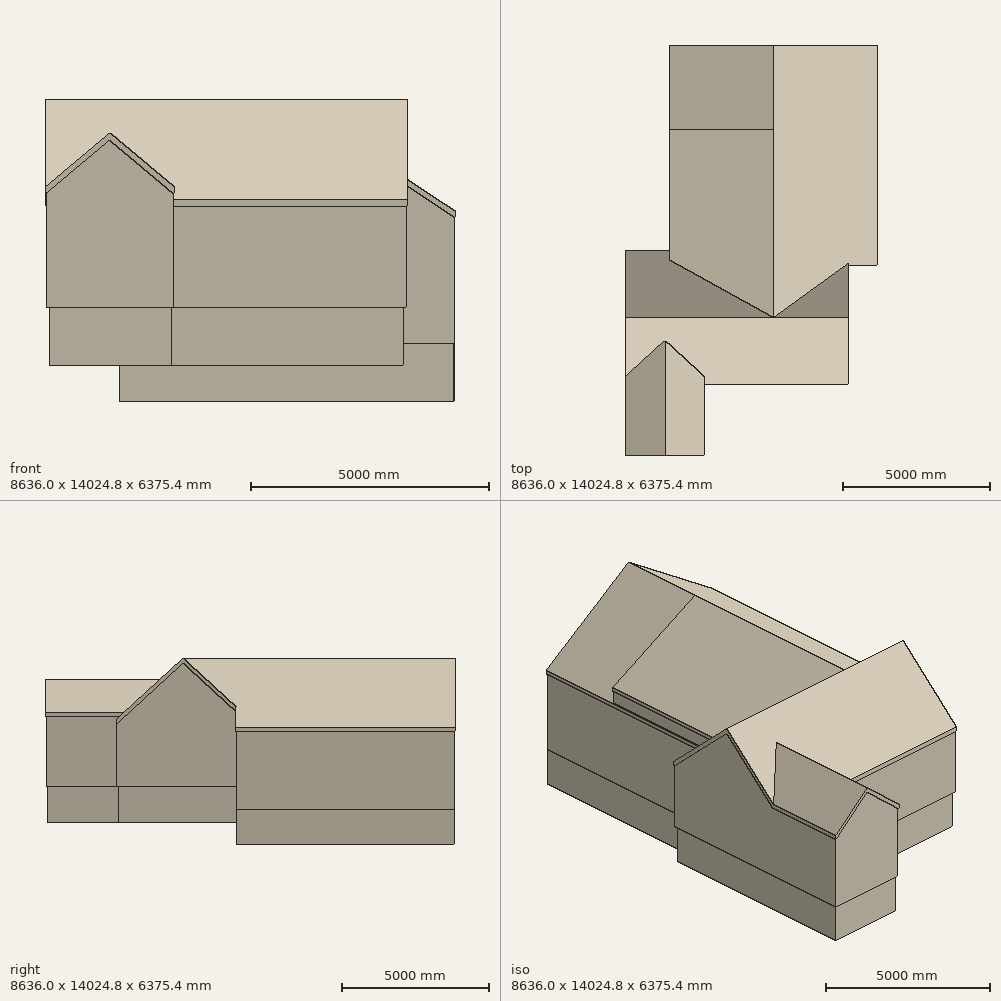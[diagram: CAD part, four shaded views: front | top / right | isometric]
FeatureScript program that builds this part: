
annotation { "Feature Type Name" : "Feature", "Feature Type Description" : "" }
export const myFeature = defineFeature(function(context is Context, id is Id, definition is map)
    precondition{}
    {
        {
            var Q0;
            Q0=qCreatedBy(makeId("Front.planeOp"),FACE);
            var sketch = newSketch(context, id + "F0", { "sketchPlane" : qUnion([Q0])});
            skLineSegment(sketch, "E0", {"start": v(0, 0) * mm, "end": v(0, 2540) * mm});
            skLineSegment(sketch, "E1", {"start": v(0, 2540) * mm, "end": v(1362.17, 3683) * mm});
            skLineSegment(sketch, "E2", {"start": v(1362.17, 3683) * mm, "end": v(2724.35, 2540) * mm});
            skLineSegment(sketch, "E3", {"start": v(2724.35, 2540) * mm, "end": v(2724.35, 0) * mm});
            skLineSegment(sketch, "E4", {"start": v(2724.35, 0) * mm, "end": v(0, 0) * mm});
            skSolve(sketch);
        }
        {
            var Q0;
            Q0 = qSketchRegion(id + "F0", true);
            extrude(context, id + "F1", {"entities" : qUnion([Q0]), "oppositeDirection" : true, "depth" : 3911.6 * mm});
        }
        {
            var Q0;
            Q0=makeQuery(id+"F1.opExtrude","SWEPT_FACE",FACE,{"disambiguationData":[OSD([sQuery(id+"F0.wireOp",EDGE,"E0")])]});
            var sketch = newSketch(context, id + "F2", { "sketchPlane" : qUnion([Q0])});
            skLineSegment(sketch, "E5", {"start": v(-7014.4, 2286) * mm, "end": v(-7014.4, 0) * mm});
            skLineSegment(sketch, "E6", {"start": v(-7014.4, 0) * mm, "end": v(-2413, 0) * mm});
            skLineSegment(sketch, "E7", {"start": v(-2413, 0) * mm, "end": v(-2413, 2286) * mm});
            skLineSegment(sketch, "E8", {"start": v(-2413, 2286) * mm, "end": v(-4713.7, 4394.2) * mm});
            skLineSegment(sketch, "E9", {"start": v(-4713.7, 4394.2) * mm, "end": v(-7014.4, 2286) * mm});
            skSolve(sketch);
        }
        {
            var Q0;
            Q0 = qSketchRegion(id + "F2", true);
            extrude(context, id + "F3", {"entities" : qUnion([Q0]), "operationType" : NewBodyOperationType.ADD, "oppositeDirection" : true, "depth" : 7620 * mm});
        }
        {
            var Q0;
            Q0=makeQuery(id+"F3.opExtrude","SWEPT_FACE",FACE,{"disambiguationData":[OSD([sQuery(id+"F2.wireOp",EDGE,"E5")])]});
            var sketch = newSketch(context, id + "F4", { "sketchPlane" : qUnion([Q0])});
            skLineSegment(sketch, "E10", {"start": v(-1524, -762) * mm, "end": v(-1524, 2032) * mm});
            skLineSegment(sketch, "E11", {"start": v(-1524, 2032) * mm, "end": v(-5080, 4394.2) * mm});
            skLineSegment(sketch, "E12", {"start": v(-5080, 4394.2) * mm, "end": v(-8636, 2032) * mm});
            skLineSegment(sketch, "E13", {"start": v(-8636, 2032) * mm, "end": v(-8636, -762) * mm});
            skLineSegment(sketch, "E14", {"start": v(-8636, -762) * mm, "end": v(-1524, -762) * mm});
            skSolve(sketch);
        }
        {
            var Q0;
            Q0 = qSketchRegion(id + "F4", true);
            var Q1;
            Q1=makeQuery(id+"F3.opExtrude","CAP_VERTEX",VERTEX,{"disambiguationData":[OSD([sQuery(id+"F2.wireOp",EDGE,"zL3uoyGX-favN-0fO6-DJR6-y5zJvDEcZm2G"),sQuery(id+"F2.wireOp",EDGE,"UiKADa09-KCoQ-Akzb-1IEs-Xu5JY1OC5VxY")])],"isStart":false});
            extrude(context, id + "F5", {"entities" : qUnion([Q0]), "operationType" : NewBodyOperationType.ADD, "depth" : 7010.4 * mm});
        }
        {
            var Q0;
            Q0=makeQuery(id+"F5.opExtrude","CAP_FACE",FACE,{"disambiguationData":[OSD([sQuery(id+"F4.wireOp",EDGE,"E10"),sQuery(id+"F4.wireOp",EDGE,"E11"),sQuery(id+"F4.wireOp",EDGE,"E12"),sQuery(id+"F4.wireOp",EDGE,"E13"),sQuery(id+"F4.wireOp",EDGE,"E14")])],"isStart":true});
            extrude(context, id + "F6", {"entities" : qUnion([Q0]), "operationType" : NewBodyOperationType.ADD, "depth" : 508 * mm});
        }
        {
            var Q0;
            {var subQ0=sQuery(id+"F4.wireOp",EDGE,"E12");var subQ1=sQuery(id+"F4.wireOp",EDGE,"E11");Q0=makeQuery(id+"F6.boolean.opBoolean","SPLIT",FACE,{"disambiguationData":[TD([makeQuery(id+"F3.opExtrude","SWEPT_FACE",FACE,{"disambiguationData":[OSD([sQuery(id+"F2.wireOp",EDGE,"E9")])]})])],"derivedFrom":makeQuery(id+"F6.opExtrude","CAP_FACE",FACE,{"disambiguationData":[OSD([sQuery(id+"F4.wireOp",EDGE,"E10"),subQ1,subQ0,sQuery(id+"F4.wireOp",EDGE,"E13"),sQuery(id+"F4.wireOp",EDGE,"E14")])],"isStart":false})});}
            var Q1;
            Q1=makeQuery(id+"F3.opExtrude","CAP_VERTEX",VERTEX,{"disambiguationData":[OSD([sQuery(id+"F2.wireOp",EDGE,"E8"),sQuery(id+"F2.wireOp",EDGE,"E9")])],"isStart":false});
            extrude(context, id + "F7", {"entities" : qUnion([Q0]), "operationType" : NewBodyOperationType.ADD, "endBound" : BoundingType.UP_TO_VERTEX, "endBoundEntityVertex" : qUnion([Q1]), "depth" : 25.4 * mm});
        }
        {
            var Q0;
            Q0=makeQuery(id+"F3.boolean.opBoolean","MERGE",FACE,{"derivedFrom":[makeQuery(id+"F1.opExtrude","SWEPT_FACE",FACE,{"disambiguationData":[OSD([sQuery(id+"F0.wireOp",EDGE,"E0")])]}),makeQuery(id+"F3.opExtrude","CAP_FACE",FACE,{"disambiguationData":[OSD([sQuery(id+"F2.wireOp",EDGE,"E5"),sQuery(id+"F2.wireOp",EDGE,"E6"),sQuery(id+"F2.wireOp",EDGE,"E7"),sQuery(id+"F2.wireOp",EDGE,"E8"),sQuery(id+"F2.wireOp",EDGE,"E9")])],"isStart":true})]});
            var sketch = newSketch(context, id + "F8", { "sketchPlane" : qUnion([Q0])});
            skLineSegment(sketch, "E15", {"start": v(-7014.4, 2113.74) * mm, "end": v(-4713.7, 4221.94) * mm});
            skLineSegment(sketch, "E16", {"start": v(-4713.7, 4221.94) * mm, "end": v(-2739.58, 2413) * mm});
            skLineSegment(sketch, "E17", {"start": v(-2739.58, 2413) * mm, "end": v(0, 2413) * mm});
            skSolve(sketch);
        }
        {
            var Q0;
            {var subQ3=sQuery(id+"F8.wireOp",EDGE,"E15");Q0=makeQuery(id+"F8.imprint","IMPRINT",FACE,{"disambiguationData":[TD([[makeQuery(id+"F8.imprint","IMPRINT",EDGE,{"derivedFrom":subQ3}),-1.0]])]});}
            extrude(context, id + "F9", {"entities" : qUnion([Q0]), "operationType" : NewBodyOperationType.REMOVE, "oppositeDirection" : true, "depth" : 25.4 * mm});
        }
        {
            var Q0;
            Q0=makeQuery(id+"F1.opExtrude","CAP_FACE",FACE,{"disambiguationData":[OSD([sQuery(id+"F0.wireOp",EDGE,"E0"),sQuery(id+"F0.wireOp",EDGE,"E1"),sQuery(id+"F0.wireOp",EDGE,"E2"),sQuery(id+"F0.wireOp",EDGE,"E3"),sQuery(id+"F0.wireOp",EDGE,"E4")])],"isStart":true});
            var sketch = newSketch(context, id + "F10", { "sketchPlane" : qUnion([Q0])});
            skLineSegment(sketch, "E18", {"start": v(25.4, 2413) * mm, "end": v(1351.76, 3525.95) * mm});
            skLineSegment(sketch, "E19", {"start": v(1351.76, 3525.95) * mm, "end": v(2678.12, 2413) * mm});
            skLineSegment(sketch, "E20", {"start": v(2678.12, 2413) * mm, "end": v(2724.35, 2413) * mm});
            skSolve(sketch);
        }
        {
            var Q0;
            Q0=makeQuery(id+"F10.imprint","IMPRINT",FACE,{"disambiguationData":[TD([[makeQuery(id+"F10.imprint","IMPRINT",EDGE,{"derivedFrom":sQuery(id+"F10.wireOp",EDGE,"E18")}),-1.0]])]});
            extrude(context, id + "F11", {"entities" : qUnion([Q0]), "operationType" : NewBodyOperationType.REMOVE, "oppositeDirection" : true, "depth" : 25.4 * mm});
        }
        {
            var Q0;
            Q0=makeQuery(id+"F1.opExtrude","SWEPT_FACE",FACE,{"disambiguationData":[OSD([sQuery(id+"F0.wireOp",EDGE,"E3")])]});
            var sketch = newSketch(context, id + "F12", { "sketchPlane" : qUnion([Q0])});
            skLineSegment(sketch, "E21", {"start": v(25.4, 2413) * mm, "end": v(2551.6, 2413) * mm});
            skSolve(sketch);
        }
        {
            var Q0;
            {var subQ3=sQuery(id+"F12.wireOp",EDGE,"E21");Q0=makeQuery(id+"F12.imprint","IMPRINT",FACE,{"disambiguationData":[TD([[makeQuery(id+"F12.imprint","IMPRINT",EDGE,{"derivedFrom":subQ3}),-1.0]])]});}
            var Q1;
            Q1 = qSketchRegion(id + "F12", true);
            extrude(context, id + "F13", {"entities" : qUnion([Q0, Q1]), "operationType" : NewBodyOperationType.REMOVE, "oppositeDirection" : true, "depth" : 25.4 * mm});
        }
        {
            var Q0;
            {var subQ0=sQuery(id+"F2.wireOp",EDGE,"E7");Q0=makeQuery(id+"F13.boolean.opBoolean","MERGE",FACE,{"derivedFrom":[makeQuery(id+"F3.opExtrude","SWEPT_FACE",FACE,{"disambiguationData":[OSD([subQ0])]}),makeQuery(id+"F13.opExtrude","SWEPT_FACE",FACE,{"disambiguationData":[OSD([sQuery(id+"F0.wireOp",EDGE,"E3"),subQ0])]})]});}
            var sketch = newSketch(context, id + "F14", { "sketchPlane" : qUnion([Q0])});
            skLineSegment(sketch, "E22", {"start": v(2698.95, 2133.6) * mm, "end": v(7620, 2133.6) * mm});
            skSolve(sketch);
        }
        {
            var Q0;
            {var subQ0=sQuery(id+"F14.wireOp",EDGE,"E22");Q0=makeQuery(id+"F14.imprint","IMPRINT",FACE,{"disambiguationData":[TD([[makeQuery(id+"F14.imprint","IMPRINT",EDGE,{"derivedFrom":subQ0}),-1.0]])]});}
            extrude(context, id + "F15", {"entities" : qUnion([Q0]), "operationType" : NewBodyOperationType.REMOVE, "oppositeDirection" : true, "depth" : 25.4 * mm});
        }
        {
            var Q0;
            Q0=makeQuery(id+"F3.opExtrude","CAP_FACE",FACE,{"disambiguationData":[OSD([sQuery(id+"F2.wireOp",EDGE,"E5"),sQuery(id+"F2.wireOp",EDGE,"E6"),sQuery(id+"F2.wireOp",EDGE,"E7"),sQuery(id+"F2.wireOp",EDGE,"E8"),sQuery(id+"F2.wireOp",EDGE,"E9")])],"isStart":false});
            var sketch = newSketch(context, id + "F16", { "sketchPlane" : qUnion([Q0])});
            skLineSegment(sketch, "E23", {"start": v(2438.4, 2133.6) * mm, "end": v(4715.56, 4220.23) * mm});
            skLineSegment(sketch, "E24", {"start": v(4715.56, 4220.23) * mm, "end": v(6506.4, 2579.24) * mm});
            skSolve(sketch);
        }
        {
            var Q0;
            Q0=makeQuery(id+"F16.imprint","IMPRINT",FACE,{"disambiguationData":[TD([[makeQuery(id+"F16.imprint","IMPRINT",EDGE,{"derivedFrom":sQuery(id+"F16.wireOp",EDGE,"E23")}),-1.0]])]});
            extrude(context, id + "F17", {"entities" : qUnion([Q0]), "operationType" : NewBodyOperationType.REMOVE, "oppositeDirection" : true, "depth" : 25.4 * mm});
        }
        {
            var Q0;
            {var subQ0=sQuery(id+"F4.wireOp",EDGE,"E13");Q0=makeQuery(id+"F6.boolean.opBoolean","MERGE",FACE,{"derivedFrom":[makeQuery(id+"F5.opExtrude","SWEPT_FACE",FACE,{"disambiguationData":[OSD([subQ0])]}),makeQuery(id+"F6.opExtrude","SWEPT_FACE",FACE,{"disambiguationData":[OSD([subQ0])]})]});}
            var sketch = newSketch(context, id + "F18", { "sketchPlane" : qUnion([Q0])});
            skLineSegment(sketch, "E25", {"start": v(6506.4, 1905) * mm, "end": v(14024.8, 1905) * mm});
            skSolve(sketch);
        }
        {
            var Q0;
            {var subQ0=sQuery(id+"F18.wireOp",EDGE,"E25");Q0=makeQuery(id+"F18.imprint","IMPRINT",FACE,{"disambiguationData":[TD([[makeQuery(id+"F18.imprint","IMPRINT",EDGE,{"derivedFrom":subQ0}),-1.0]])]});}
            extrude(context, id + "F19", {"entities" : qUnion([Q0]), "operationType" : NewBodyOperationType.REMOVE, "oppositeDirection" : true, "depth" : 25.4 * mm});
        }
        {
            var Q0;
            {var subQ0=sQuery(id+"F4.wireOp",EDGE,"E14");var subQ1=sQuery(id+"F4.wireOp",EDGE,"E13");var subQ2=sQuery(id+"F4.wireOp",EDGE,"E12");var subQ3=sQuery(id+"F4.wireOp",EDGE,"E11");var subQ4=sQuery(id+"F4.wireOp",EDGE,"E10");var subQ5=sQuery(id+"F2.wireOp",EDGE,"E9");var subQ6=sQuery(id+"F2.wireOp",EDGE,"E8");var subQ7=sQuery(id+"F2.wireOp",EDGE,"E7");var subQ8=sQuery(id+"F2.wireOp",EDGE,"E6");var subQ9=sQuery(id+"F2.wireOp",EDGE,"E5");Q0=makeQuery(id+"F17.boolean.opBoolean","MERGE",FACE,{"derivedFrom":[makeQuery(id+"F6.boolean.opBoolean","SPLIT",FACE,{"disambiguationData":[TD([makeQuery(id+"F1.opExtrude","SWEPT_FACE",FACE,{"disambiguationData":[OSD([sQuery(id+"F0.wireOp",EDGE,"E4")])]})])],"derivedFrom":makeQuery(id+"F6.opExtrude","CAP_FACE",FACE,{"disambiguationData":[OSD([subQ4,subQ3,subQ2,subQ1,subQ0])],"isStart":false})}),makeQuery(id+"F17.opExtrude","SWEPT_FACE",FACE,{"disambiguationData":[OSD([subQ9,subQ8,subQ7,subQ6,subQ5,subQ4,subQ3,subQ2,subQ1,subQ0])]})]});}
            var sketch = newSketch(context, id + "F20", { "sketchPlane" : qUnion([Q0])});
            skLineSegment(sketch, "E26", {"start": v(8610.6, 1905) * mm, "end": v(7594.6, 2579.24) * mm});
            skPoint(sketch, "E26.endSnap0", {"position": v(7607.3, 2579.24) * mm});
            skSolve(sketch);
        }
        {
            var Q0;
            Q0=makeQuery(id+"F20.imprint","IMPRINT",FACE,{"disambiguationData":[TD([[makeQuery(id+"F20.imprint","IMPRINT",EDGE,{"derivedFrom":sQuery(id+"F20.wireOp",EDGE,"E26")}),1.0]])]});
            extrude(context, id + "F21", {"entities" : qUnion([Q0]), "operationType" : NewBodyOperationType.REMOVE, "oppositeDirection" : true, "depth" : 25.4 * mm});
        }
        {
            var Q0;
            {var subQ0=sQuery(id+"F4.wireOp",EDGE,"E10");Q0=makeQuery(id+"F6.boolean.opBoolean","MERGE",FACE,{"derivedFrom":[makeQuery(id+"F5.opExtrude","SWEPT_FACE",FACE,{"disambiguationData":[OSD([subQ0])]}),makeQuery(id+"F6.opExtrude","SWEPT_FACE",FACE,{"disambiguationData":[OSD([subQ0])]})]});}
            var sketch = newSketch(context, id + "F22", { "sketchPlane" : qUnion([Q0])});
            skLineSegment(sketch, "E27", {"start": v(-14024.8, 1905) * mm, "end": v(-7014.4, 1905) * mm});
            skSolve(sketch);
        }
        {
            var Q0;
            {var subQ5=sQuery(id+"F22.wireOp",EDGE,"E27");Q0=makeQuery(id+"F22.imprint","IMPRINT",FACE,{"disambiguationData":[TD([[makeQuery(id+"F22.imprint","IMPRINT",EDGE,{"derivedFrom":subQ5}),-1.0]])]});}
            extrude(context, id + "F23", {"entities" : qUnion([Q0]), "operationType" : NewBodyOperationType.REMOVE, "oppositeDirection" : true, "depth" : 25.4 * mm});
        }
        {
            var Q0;
            Q0=makeQuery(id+"F5.opExtrude","CAP_FACE",FACE,{"disambiguationData":[OSD([sQuery(id+"F4.wireOp",EDGE,"E10"),sQuery(id+"F4.wireOp",EDGE,"E11"),sQuery(id+"F4.wireOp",EDGE,"E12"),sQuery(id+"F4.wireOp",EDGE,"E13"),sQuery(id+"F4.wireOp",EDGE,"E14")])],"isStart":false});
            var sketch = newSketch(context, id + "F24", { "sketchPlane" : qUnion([Q0])});
            skLineSegment(sketch, "E28", {"start": v(-8610.6, 1905) * mm, "end": v(-5080, 4250.33) * mm});
            skLineSegment(sketch, "E29", {"start": v(-5080, 4250.33) * mm, "end": v(-1549.4, 1905) * mm});
            skSolve(sketch);
        }
        {
            var Q0;
            Q0=makeQuery(id+"F24.imprint","IMPRINT",FACE,{"disambiguationData":[TD([[makeQuery(id+"F24.imprint","IMPRINT",EDGE,{"derivedFrom":sQuery(id+"F24.wireOp",EDGE,"E28")}),-1.0]])]});
            extrude(context, id + "F25", {"entities" : qUnion([Q0]), "operationType" : NewBodyOperationType.REMOVE, "oppositeDirection" : true, "depth" : 25.4 * mm});
        }
        {
            var Q0;
            {var subQ0=sQuery(id+"F4.wireOp",EDGE,"E10");var subQ1=sQuery(id+"F2.wireOp",EDGE,"E5");var subQ2=makeQuery(id+"F3.opExtrude","SWEPT_FACE",FACE,{"disambiguationData":[OSD([subQ1])]});var subQ3=makeQuery(id+"F5.boolean.opBoolean","SPLIT",EDGE,{"disambiguationData":[topologyDisambiguationEdgeConnected([subQ2])],"derivedFrom":makeQuery(id+"F5.opExtrude","CAP_EDGE",EDGE,{"disambiguationData":[OSD([subQ0])],"isStart":true})});Q0=makeQuery(id+"F23.boolean.opBoolean","MERGE",FACE,{"derivedFrom":[subQ2,makeQuery(id+"F23.opExtrude","SWEPT_FACE",FACE,{"disambiguationData":[OSD([subQ0]),TDD([makeQuery(id+"F22.imprint","IMPRINT",EDGE,{"disambiguationData":[TD([[makeQuery(id+"F22.imprint","INTERSECT",VERTEX,{"derivedFrom":[subQ3,sQuery(id+"F22.wireOp",EDGE,"E27")]}),1.0]])],"derivedFrom":subQ3})])]})]});}
            var sketch = newSketch(context, id + "F26", { "sketchPlane" : qUnion([Q0])});
            skLineSegment(sketch, "E30", {"start": v(-1715.18, 2159) * mm, "end": v(0, 2159) * mm});
            skSolve(sketch);
        }
        {
            var Q0;
            {var subQ12=sQuery(id+"F26.wireOp",EDGE,"E30");Q0=makeQuery(id+"F26.imprint","IMPRINT",FACE,{"disambiguationData":[TD([[makeQuery(id+"F26.imprint","IMPRINT",EDGE,{"derivedFrom":subQ12}),-1.0]])]});}
            extrude(context, id + "F27", {"entities" : qUnion([Q0]), "operationType" : NewBodyOperationType.REMOVE, "oppositeDirection" : true, "depth" : 25.4 * mm});
        }
        {
            var Q0;
            Q0=makeQuery(id+"F3.boolean.opBoolean","MERGE",FACE,{"derivedFrom":[makeQuery(id+"F1.opExtrude","SWEPT_FACE",FACE,{"disambiguationData":[OSD([sQuery(id+"F0.wireOp",EDGE,"E0")])]}),makeQuery(id+"F3.opExtrude","CAP_FACE",FACE,{"disambiguationData":[OSD([sQuery(id+"F2.wireOp",EDGE,"E5"),sQuery(id+"F2.wireOp",EDGE,"E6"),sQuery(id+"F2.wireOp",EDGE,"E7"),sQuery(id+"F2.wireOp",EDGE,"E8"),sQuery(id+"F2.wireOp",EDGE,"E9")])],"isStart":true})]});
            var sketch = newSketch(context, id + "F28", { "sketchPlane" : qUnion([Q0])});
            skLineSegment(sketch, "E31", {"start": v(-6989, 2159) * mm, "end": v(-6965, 2159) * mm});
            skSolve(sketch);
        }
        {
            var Q0;
            {var subQ0=sQuery(id+"F28.wireOp",EDGE,"E31");Q0=makeQuery(id+"F28.imprint","IMPRINT",FACE,{"disambiguationData":[TD([[makeQuery(id+"F28.imprint","IMPRINT",EDGE,{"derivedFrom":subQ0}),-1.0]])]});}
            var Q1;
            Q1=makeQuery(id+"F9.boolean.opBoolean","COPY",FACE,{"derivedFrom":makeQuery(id+"F9.opExtrude","CAP_FACE",FACE,{"disambiguationData":[OSD([sQuery(id+"F0.wireOp",EDGE,"E0"),sQuery(id+"F0.wireOp",EDGE,"E4"),sQuery(id+"F2.wireOp",EDGE,"E5"),sQuery(id+"F2.wireOp",EDGE,"E6"),sQuery(id+"F8.wireOp",EDGE,"E15"),sQuery(id+"F8.wireOp",EDGE,"E16"),sQuery(id+"F8.wireOp",EDGE,"E17")])],"isStart":false})});
            extrude(context, id + "F29", {"entities" : qUnion([Q0]), "operationType" : NewBodyOperationType.REMOVE, "endBound" : BoundingType.UP_TO_SURFACE, "oppositeDirection" : true, "endBoundEntityFace" : qUnion([Q1]), "depth" : 25.4 * mm});
        }
        {
            var Q0;
            Q0=makeQuery(id+"F25.boolean.opBoolean","COPY",FACE,{"derivedFrom":makeQuery(id+"F25.opExtrude","CAP_FACE",FACE,{"disambiguationData":[OSD([sQuery(id+"F4.wireOp",EDGE,"E10"),sQuery(id+"F4.wireOp",EDGE,"E13"),sQuery(id+"F4.wireOp",EDGE,"E14"),sQuery(id+"F24.wireOp",EDGE,"E28"),sQuery(id+"F24.wireOp",EDGE,"E29")])],"isStart":false})});
            cPlane(context, id + "F30", {"entities" : qUnion([Q0]), "cplaneType" : CPlaneType.OFFSET, "offset" : 2844.8 * mm, "oppositeDirection" : true, "width" : 152.4 * mm, "height" : 152.4 * mm});
        }
        {
            var Q0;
            Q0=qCreatedBy(id+"F30.planeOp",FACE);
            var sketch = newSketch(context, id + "F31", { "sketchPlane" : qUnion([Q0])});
            skLineSegment(sketch, "E32", {"start": v(-5080, 4394.2) * mm, "end": v(-1524, 2590.8) * mm});
            skLineSegment(sketch, "E33", {"start": v(-1524, 2590.8) * mm, "end": v(-1524, 2463.8) * mm});
            skLineSegment(sketch, "E34", {"start": v(-1524, 2463.8) * mm, "end": v(-1549.4, 2463.8) * mm});
            skLineSegment(sketch, "E35", {"start": v(-1549.4, 2463.8) * mm, "end": v(-1549.4, 2048.87) * mm});
            skLineSegment(sketch, "E36", {"start": v(-1549.4, 2048.87) * mm, "end": v(-5080, 4394.2) * mm});
            skSolve(sketch);
        }
        {
            var Q0;
            Q0=makeQuery(id+"F31.imprint","IMPRINT",FACE,{"disambiguationData":[TD([[makeQuery(id+"F31.imprint","IMPRINT",EDGE,{"derivedFrom":sQuery(id+"F31.wireOp",EDGE,"E32")}),-1.0]])]});
            var Q1;
            Q1=makeQuery(id+"F7.opExtrude","CAP_VERTEX",VERTEX,{"disambiguationData":[OSD([sQuery(id+"F4.wireOp",EDGE,"E11"),sQuery(id+"F4.wireOp",EDGE,"E12"),dummyQuery(id+"F7.vertexPlane.planeOp",FACE)])],"isStart":false});
            extrude(context, id + "F32", {"entities" : qUnion([Q0]), "operationType" : NewBodyOperationType.ADD, "endBound" : BoundingType.UP_TO_VERTEX, "oppositeDirection" : true, "endBoundEntityVertex" : qUnion([Q1]), "depth" : 4892.04 * mm});
        }
        {
            var Q0;
            {var subQ0=sQuery(id+"F4.wireOp",EDGE,"E14");Q0=makeQuery(id+"F6.boolean.opBoolean","MERGE",FACE,{"derivedFrom":[makeQuery(id+"F5.opExtrude","SWEPT_FACE",FACE,{"disambiguationData":[OSD([subQ0])]}),makeQuery(id+"F6.opExtrude","SWEPT_FACE",FACE,{"disambiguationData":[OSD([subQ0])]})]});}
            var sketch = newSketch(context, id + "F33", { "sketchPlane" : qUnion([Q0])});
            skLineSegment(sketch, "E37.0", {"start": v(1600.2, -13948.6) * mm, "end": v(8559.8, -13948.6) * mm});
            skLineSegment(sketch, "E37.1", {"start": v(1600.2, -6582.6) * mm, "end": v(1600.2, -13948.6) * mm});
            skLineSegment(sketch, "E37.2", {"start": v(8559.8, -6582.6) * mm, "end": v(1600.2, -6582.6) * mm});
            skLineSegment(sketch, "E37.3", {"start": v(8559.8, -13948.6) * mm, "end": v(8559.8, -6582.6) * mm});
            skLineSegment(sketch, "E38.0", {"start": v(1555.75, -13993.04) * mm, "end": v(8604.25, -13993.04) * mm});
            skLineSegment(sketch, "E38.1", {"start": v(1555.75, -6538.14) * mm, "end": v(1555.75, -13993.04) * mm});
            skLineSegment(sketch, "E38.2", {"start": v(8604.25, -6538.14) * mm, "end": v(1555.75, -6538.14) * mm});
            skLineSegment(sketch, "E38.3", {"start": v(8604.25, -13993.04) * mm, "end": v(8604.25, -6538.14) * mm});
            skSolve(sketch);
        }
        {
            var Q0;
            Q0 = qSketchRegion(id + "F33", true);
            extrude(context, id + "F34", {"entities" : qUnion([Q0]), "operationType" : NewBodyOperationType.ADD, "depth" : 1219.2 * mm});
        }
        {
            var Q0;
            {var subQ0=sQuery(id+"F2.wireOp",EDGE,"E6");var subQ1=sQuery(id+"F2.wireOp",EDGE,"E5");var subQ2=sQuery(id+"F0.wireOp",EDGE,"E4");Q0=makeQuery(id+"F23.boolean.opBoolean","MERGE",FACE,{"derivedFrom":[makeQuery(id+"F21.boolean.opBoolean","MERGE",FACE,{"derivedFrom":[makeQuery(id+"F3.boolean.opBoolean","MERGE",FACE,{"derivedFrom":[makeQuery(id+"F1.opExtrude","SWEPT_FACE",FACE,{"disambiguationData":[OSD([subQ2])]}),makeQuery(id+"F3.opExtrude","SWEPT_FACE",FACE,{"disambiguationData":[OSD([subQ0])]})]}),makeQuery(id+"F21.opExtrude","SWEPT_FACE",FACE,{"disambiguationData":[OSD([subQ1,subQ0])]})]}),makeQuery(id+"F23.opExtrude","SWEPT_FACE",FACE,{"disambiguationData":[OSD([subQ2,subQ1,subQ0,sQuery(id+"F4.wireOp",EDGE,"E10"),sQuery(id+"F4.wireOp",EDGE,"E11"),sQuery(id+"F4.wireOp",EDGE,"E12"),sQuery(id+"F4.wireOp",EDGE,"E13"),sQuery(id+"F4.wireOp",EDGE,"E14")])]})]});}
            var sketch = newSketch(context, id + "F35", { "sketchPlane" : qUnion([Q0])});
            skLineSegment(sketch, "E39.0", {"start": v(76.2, -76.2) * mm, "end": v(76.2, -6938.2) * mm});
            skLineSegment(sketch, "E39.1", {"start": v(2648.15, -76.2) * mm, "end": v(76.2, -76.2) * mm});
            skLineSegment(sketch, "E39.2", {"start": v(76.2, -6938.2) * mm, "end": v(7543.8, -6938.2) * mm});
            skLineSegment(sketch, "E39.3", {"start": v(2648.15, -2489.2) * mm, "end": v(2648.15, -76.2) * mm});
            skLineSegment(sketch, "E39.6", {"start": v(7543.8, -6938.2) * mm, "end": v(7543.8, -2489.2) * mm});
            skLineSegment(sketch, "E39.7", {"start": v(7543.8, -2489.2) * mm, "end": v(2648.15, -2489.2) * mm});
            skSolve(sketch);
        }
        {
            var Q0;
            Q0 = qSketchRegion(id + "F35", true);
            extrude(context, id + "F36", {"entities" : qUnion([Q0]), "operationType" : NewBodyOperationType.ADD, "depth" : 1219.2 * mm});
        }
    });
